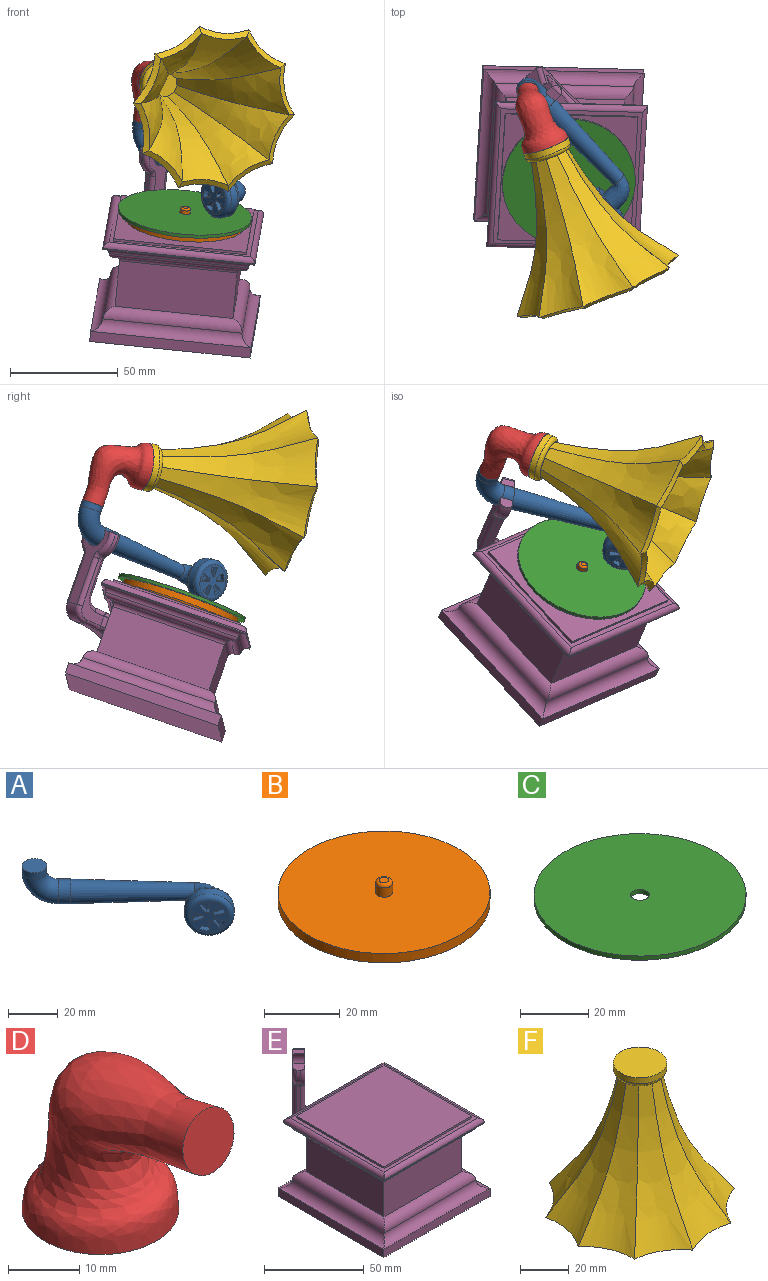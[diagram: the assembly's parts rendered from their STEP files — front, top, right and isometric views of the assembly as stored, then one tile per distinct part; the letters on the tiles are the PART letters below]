
ASSEMBLY  parts=6 mates=4
PART A: 36 faces, bbox 59.3x74.5x23.5 mm
  f0: plane 16x11.31mm, normal (-0.71,-0.71,0), area 140.5mm2, adj f9,f11,f12,f13,f14,f16,f17,f18
  f1: plane 10x10mm, normal (0,0,1), area 78.5mm2, adj f2
  f2: cylinder r=5mm len=10mm, axis (0,0,-1), area 89.1mm2, adj f1,f3
  f3: torus R=9.8mm, axis (-0.71,-0.71,0), area 483.5mm2, adj f2,f4
  f4: cylinder r=5mm len=10.53mm, axis (0.71,-0.71,0), area 153.6mm2, adj f3,f5
  f5: cone r=5mm half-angle=1.7deg, axis (-0.71,0.71,0), area 1335.8mm2, adj f4,f10
  f6: plane 16x11.31mm, normal (0.71,0.71,0), area 122.5mm2, adj f8,f10
  f7: cylinder r=10mm len=20mm, axis (0.71,0.71,0), area 251.3mm2, adj f8,f9
  f8: torus R=8mm, axis (0.71,0.71,0), area 183mm2, adj f6,f7
  f9: torus R=8mm, axis (0.71,0.71,0), area 183mm2, adj f0,f7
  f10: bspline ~17.32x14.96mm, area 372.1mm2, adj f5,f6
  f11: plane 3.64x3.57mm, normal (0.57,-0.57,0.59), area 10.8mm2, adj f0,f12,f14,f15
  f12: cylinder r=2.3mm len=2.55mm, axis (-0.71,-0.71,0), area 3.1mm2, adj f0,f11,f13,f15
  f13: plane 4.5x1.7mm, normal (-0.71,0.71,0), area 10.8mm2, adj f0,f12,f14,f15
  f14: cylinder r=6.8mm len=4.42mm, axis (-0.71,-0.71,0), area 9.9mm2, adj f0,f11,f13,f15
  f15: plane 4.89x2.72mm, normal (-0.71,-0.71,0), area 12.1mm2, adj f11,f12,f13,f14
  f16: plane 4.5x1.7mm, normal (-0.71,0.71,0), area 10.8mm2, adj f0,f17,f19,f20
  f17: cylinder r=2.3mm len=2.55mm, axis (-0.71,-0.71,0), area 3.1mm2, adj f0,f16,f18,f20
  f18: plane 3.64x3.57mm, normal (0.57,-0.57,-0.59), area 10.8mm2, adj f0,f17,f19,f20
  f19: cylinder r=6.8mm len=4.42mm, axis (-0.71,-0.71,0), area 9.9mm2, adj f0,f16,f18,f20
  f20: plane 4.89x2.72mm, normal (-0.71,-0.71,0), area 12.1mm2, adj f16,f17,f18,f19
  f21: plane 4.72x4.72mm, normal (-0.22,0.22,0.95), area 10.8mm2, adj f0,f22,f24,f25
  f22: cylinder r=2.3mm len=1.76mm, axis (-0.71,-0.71,0), area 3.1mm2, adj f0,f21,f23,f25
  f23: plane 4.72x4.72mm, normal (-0.22,0.22,-0.95), area 10.8mm2, adj f0,f22,f24,f25
  f24: cylinder r=6.8mm len=4.04mm, axis (-0.71,-0.71,0), area 9.9mm2, adj f0,f21,f23,f25
  f25: plane 4.04x3.24mm, normal (-0.71,-0.71,0), area 12.1mm2, adj f21,f22,f23,f24
  f26: plane 4.72x4.72mm, normal (-0.22,0.22,-0.95), area 10.8mm2, adj f0,f27,f29,f30
  f27: cylinder r=2.3mm len=2.22mm, axis (-0.71,-0.71,0), area 3.1mm2, adj f0,f26,f28,f30
  f28: plane 3.64x3.57mm, normal (0.57,-0.57,0.59), area 10.8mm2, adj f0,f27,f29,f30
  f29: cylinder r=6.8mm len=3.38mm, axis (-0.71,-0.71,0), area 9.9mm2, adj f0,f26,f28,f30
  f30: plane 4.66x3.55mm, normal (-0.71,-0.71,0), area 12.1mm2, adj f26,f27,f28,f29
  f31: plane 3.64x3.57mm, normal (0.57,-0.57,-0.59), area 10.8mm2, adj f0,f32,f34,f35
  f32: cylinder r=2.3mm len=2.22mm, axis (-0.71,-0.71,0), area 3.1mm2, adj f0,f31,f33,f35
  f33: plane 4.72x4.72mm, normal (-0.22,0.22,0.95), area 10.8mm2, adj f0,f32,f34,f35
  f34: cylinder r=6.8mm len=3.38mm, axis (-0.71,-0.71,0), area 9.9mm2, adj f0,f31,f33,f35
  f35: plane 4.66x3.55mm, normal (-0.71,-0.71,0), area 12.1mm2, adj f31,f32,f33,f34
PART B: 8 faces, bbox 56x56x8.2 mm
  f0: cylinder r=6mm len=12mm, axis (0,0,-1), area 45.2mm2, adj f1,f4
  f1: plane 12x12mm, normal (0,0,-1), area 113.1mm2, adj f0
  f2: cylinder r=28mm len=56mm, axis (0,0,-1), area 527.8mm2, adj f3,f4
  f3: plane 56x56mm, normal (0,0,1), area 2447.1mm2, adj f2,f5
  f4: plane 56x56mm, normal (0,0,-1), area 2349.9mm2, adj f0,f2
  f5: cylinder r=2.25mm len=4.5mm, axis (0,0,-1), area 42.4mm2, adj f3,f7
  f6: plane 2.5x2.5mm, normal (0,0,1), area 4.9mm2, adj f7
  f7: torus R=1.25mm, axis (0,0,1), area 18.6mm2, adj f5,f6
PART C: 4 faces, bbox 62x62x1.5 mm
  f0: cylinder r=2.75mm len=5.5mm, axis (0,0,-1), area 25.9mm2, adj f2,f3
  f1: cylinder r=31mm len=62mm, axis (0,0,-1), area 292.2mm2, adj f2,f3
  f2: plane 62x62mm, normal (0,0,1), area 2995.3mm2, adj f0,f1
  f3: plane 62x62mm, normal (0,0,-1), area 2995.3mm2, adj f0,f1
PART D: 3 faces, bbox 22x33.3x27.3 mm
  f0: plane 22x22mm, normal (0,0,-1), area 380.1mm2, adj f2
  f1: plane 10.01x9.86mm, normal (0,-0.98,0.17), area 78.5mm2, adj f2
  f2: bspline ~33.29x27.34mm, area 1810.4mm2, adj f0,f1
PART E: 88 faces, bbox 75.4x91.3x71.6 mm
  f0: plane 66x66mm, normal (0,0,1), area 512mm2, adj f35,f36,f37,f38,f39,f40,f41,f42
  f1: plane 75x5mm, normal (-1,0,0), area 375mm2, adj f2,f4,f5,f6
  f2: plane 75x5mm, normal (0,-1,0), area 375mm2, adj f1,f3,f5,f8
  f3: plane 75x5mm, normal (1,0,0), area 375mm2, adj f2,f4,f5,f9
  f4: plane 75x5mm, normal (0,1,0), area 375mm2, adj f1,f3,f5,f7
  f5: plane 75x75mm, normal (0,0,-1), area 5625mm2, adj f1,f2,f3,f4
  f6: cylinder r=5mm len=75mm, axis (0,-1,0), area 539mm2, adj f1,f7,f8,f14
  f7: cylinder r=5mm len=75mm, axis (-1,0,0), area 539mm2, adj f4,f6,f9,f15
  f8: cylinder r=5mm len=75mm, axis (1,0,0), area 539mm2, adj f2,f6,f9,f16
  f9: cylinder r=5mm len=75mm, axis (0,1,0), area 539mm2, adj f3,f7,f8,f17
  f10: plane 55x22.5mm, normal (1,0,0), area 1237.5mm2, adj f11,f13,f17,f21
  f11: plane 55x22.5mm, normal (0,1,0), area 970.8mm2, adj f10,f12,f15,f18,f68,f70,f71,f72
  f12: plane 55x22.5mm, normal (-1,0,0), area 1237.5mm2, adj f11,f13,f14,f19
  f13: plane 55x22.5mm, normal (0,-1,0), area 1237.5mm2, adj f10,f12,f16,f22
  f14: cylinder r=5mm len=65mm, axis (0,1,0), area 482mm2, adj f6,f12,f15,f16
  f15: cylinder r=5mm len=65mm, axis (1,0,0), area 482mm2, adj f7,f11,f14,f17
  f16: cylinder r=5mm len=65mm, axis (-1,0,0), area 482mm2, adj f8,f13,f14,f17
  f17: cylinder r=5mm len=65mm, axis (0,-1,0), area 482mm2, adj f9,f10,f15,f16
  f18: cylinder r=2.5mm len=60mm, axis (1,0,0), area 223.1mm2, adj f11,f19,f20,f21
  f19: cylinder r=2.5mm len=60mm, axis (0,1,0), area 223.1mm2, adj f12,f18,f22,f23
  f20: cylinder r=2.5mm len=64.98mm, axis (-1,0,0), area 233.3mm2, adj f18,f23,f24,f31
  f21: cylinder r=2.5mm len=60mm, axis (0,-1,0), area 223.1mm2, adj f10,f18,f22,f24
  f22: cylinder r=2.5mm len=60mm, axis (-1,0,0), area 223.1mm2, adj f13,f19,f21,f25
  f23: cylinder r=2.5mm len=64.98mm, axis (0,-1,0), area 233.3mm2, adj f19,f20,f25,f32
  f24: cylinder r=2.5mm len=64.98mm, axis (0,1,0), area 233.3mm2, adj f20,f21,f25,f33
  f25: cylinder r=2.5mm len=64.98mm, axis (1,0,0), area 233.3mm2, adj f22,f23,f24,f34
  f26: plane 71x0.5mm, normal (1,0,0), area 35.5mm2, adj f27,f29,f30,f35
  f27: plane 71x0.5mm, normal (0,1,0), area 35.5mm2, adj f26,f28,f30,f37
  f28: plane 71x0.5mm, normal (-1,0,0), area 35.5mm2, adj f27,f29,f30,f38
  f29: plane 71x0.5mm, normal (0,-1,0), area 35.5mm2, adj f26,f28,f30,f36
  f30: plane 71x71mm, normal (0,0,-1), area 6.5mm2, adj f26,f27,f28,f29,f31,f32,f33,f34
  f31: cylinder r=3mm len=70.95mm, axis (-1,0,0), area 298.6mm2, adj f20,f30,f32,f33
  f32: cylinder r=3mm len=70.95mm, axis (0,-1,0), area 298.6mm2, adj f23,f30,f31,f34
  f33: cylinder r=3mm len=70.95mm, axis (0,1,0), area 298.6mm2, adj f24,f30,f31,f34
  f34: cylinder r=3mm len=70.95mm, axis (1,0,0), area 298.6mm2, adj f25,f30,f32,f33
  f35: cylinder r=2.5mm len=71mm, axis (0,-1,0), area 271.7mm2, adj f0,f26,f36,f37
  f36: cylinder r=2.5mm len=71mm, axis (-1,0,0), area 271.7mm2, adj f0,f29,f35,f38
  f37: cylinder r=2.5mm len=71mm, axis (1,0,0), area 271.7mm2, adj f0,f27,f35,f38
  f38: cylinder r=2.5mm len=71mm, axis (0,1,0), area 271.7mm2, adj f0,f28,f36,f37
  f39: plane 62x1.2mm, normal (1,0,0), area 74.4mm2, adj f0,f40,f42,f43
  f40: plane 62x1.2mm, normal (0,1,0), area 74.4mm2, adj f0,f39,f41,f43
  f41: plane 62x1.2mm, normal (-1,0,0), area 74.4mm2, adj f0,f40,f42,f43
  f42: plane 62x1.2mm, normal (0,-1,0), area 74.4mm2, adj f0,f39,f41,f43
  f43: plane 62x62mm, normal (0,0,1), area 3844mm2, adj f39,f40,f41,f42
  f44: plane 15.31x11.06mm, normal (0,0,1), area 75.9mm2, adj f51,f69,f74,f79
  f45: cylinder r=59.47mm len=18.28mm, axis (-0.71,-0.71,0), area 101.3mm2, adj f48,f66,f71,f76
  f46: plane 31.84x20.25mm, normal (0.71,0.71,0), area 212.1mm2, adj f61,f62,f64,f65,f66,f67,f69,f70
  f47: plane 28.7x10.36mm, normal (-0.71,-0.71,0), area 123.1mm2, adj f75,f76,f78,f79,f80,f82,f84,f85
  f48: cylinder r=7.02mm len=9.45mm, axis (-0.71,-0.71,0), area 68.2mm2, adj f45,f49,f64,f78
  f49: plane 36.62x11.81mm, normal (-0.71,0.71,0), area 237.6mm2, adj f48,f52,f53,f54,f57,f59,f62,f80
  f50: plane 29.8x11.81mm, normal (0.71,-0.71,0), area 196.7mm2, adj f51,f52,f53,f54,f60,f63,f65,f84
  f51: cylinder r=5mm len=7.78mm, axis (-0.71,-0.71,0), area 47.1mm2, adj f44,f50,f67,f82
  f52: plane 7.62x7.62mm, normal (0,0,1), area 31.1mm2, adj f49,f50,f53,f56,f81,f87
  f53: cylinder r=5.35mm len=11.81mm, axis (-0.71,0.71,0), area 139.1mm2, adj f49,f50,f52,f54
  f54: plane 6.94x6.94mm, normal (0,0,1), area 23.1mm2, adj f49,f50,f53,f57,f58,f60
  f55: cylinder r=10.35mm len=9.77mm, axis (-0.71,0.71,0), area 22.5mm2, adj f57,f58,f60,f61
  f56: cylinder r=10.35mm len=11.53mm, axis (-0.71,0.71,0), area 26.1mm2, adj f52,f81,f85,f87
  f57: torus R=8.35mm, axis (0.71,-0.71,0), area 36.8mm2, adj f49,f54,f55,f58,f59
  f58: cylinder r=2mm len=5.57mm, axis (-0.71,0.71,0), area 11.4mm2, adj f54,f55,f57,f60
  f59: torus R=4mm, axis (0.71,-0.71,0), area 8.3mm2, adj f49,f57,f61,f62
  f60: torus R=8.35mm, axis (-0.71,0.71,0), area 36.8mm2, adj f50,f54,f55,f58,f63
  f61: cylinder r=2mm len=2.03mm, axis (-0.71,0.71,0), area 3.9mm2, adj f46,f55,f59,f63
  f62: cylinder r=2mm len=23.44mm, axis (0,0,-1), area 73.6mm2, adj f46,f49,f59,f64
  f63: torus R=4mm, axis (-0.71,0.71,0), area 8.3mm2, adj f50,f60,f61,f65
  f64: torus R=5.02mm, axis (0.71,0.71,0), area 32mm2, adj f46,f48,f62,f66
  f65: cylinder r=2mm len=16.63mm, axis (0,0,1), area 52.2mm2, adj f46,f50,f63,f67
  f66: torus R=61.47mm, axis (0.71,0.71,0), area 71mm2, adj f45,f46,f64,f68
  f67: torus R=7mm, axis (0.71,0.71,0), area 28.3mm2, adj f46,f51,f65,f69
  f68: bspline ~6.66x3.29mm, area 11.3mm2, adj f11,f66,f70,f71
  f69: cylinder r=2mm len=15.31mm, axis (-0.71,0.71,0), area 57.1mm2, adj f44,f46,f67,f72
  f70: cylinder r=2mm len=8.21mm, axis (0,0,1), area 12.9mm2, adj f11,f46,f68,f72
  f71: bspline ~8.89x3.4mm, area 24.4mm2, adj f11,f45,f68,f73
  f72: bspline ~6.64x4.7mm, area 13.9mm2, adj f11,f69,f70,f74
  f73: bspline ~6.37x5.35mm, area 22.4mm2, adj f11,f71,f75,f76
  f74: cylinder r=2mm len=8.49mm, axis (-1,0,0), area 26.7mm2, adj f11,f44,f72,f77
  f75: cylinder r=2mm len=5.08mm, axis (0,0,-1), area 23.9mm2, adj f11,f47,f73,f77
  f76: torus R=61.47mm, axis (0.71,0.71,0), area 34.5mm2, adj f45,f47,f73,f78
  f77: bspline ~5.66x4mm, area 21.5mm2, adj f11,f74,f75,f79
  f78: torus R=5.02mm, axis (0.71,0.71,0), area 32mm2, adj f47,f48,f76,f80
  f79: cylinder r=2mm len=8.23mm, axis (0.71,-0.71,0), area 22.3mm2, adj f44,f47,f77,f82
  f80: cylinder r=2mm len=23.44mm, axis (0,0,1), area 73.6mm2, adj f47,f49,f78,f83
  f81: torus R=8.35mm, axis (0.71,-0.71,0), area 39.2mm2, adj f49,f52,f56,f83
  f82: torus R=7mm, axis (0.71,0.71,0), area 28.3mm2, adj f47,f51,f79,f84
  f83: torus R=4mm, axis (0.71,-0.71,0), area 8.3mm2, adj f49,f80,f81,f85
  f84: cylinder r=2mm len=16.63mm, axis (0,0,-1), area 52.2mm2, adj f47,f50,f82,f86
  f85: cylinder r=2mm len=2.03mm, axis (-0.71,0.71,0), area 3.9mm2, adj f47,f56,f83,f86
  f86: torus R=4mm, axis (-0.71,0.71,0), area 8.3mm2, adj f50,f84,f85,f87
  f87: torus R=8.35mm, axis (-0.71,0.71,0), area 39.2mm2, adj f50,f52,f56,f86
PART F: 44 faces, bbox 89.9x89.8x78.5 mm
  f0: plane 4.7x2.76mm, normal (0,0,-1), area 1.4mm2, adj f15,f43
  f1: plane 4.97x2.24mm, normal (0,0,-1), area 1.4mm2, adj f14,f43
  f2: plane 5.3x1.24mm, normal (0,0,-1), area 1.4mm2, adj f13,f43
  f3: plane 4.06x3.64mm, normal (0,0,-1), area 1.4mm2, adj f12,f43
  f4: plane 5.4x0.8mm, normal (0,0,-1), area 1.4mm2, adj f11,f43
  f5: plane 4.7x2.76mm, normal (0,0,-1), area 1.4mm2, adj f10,f43
  f6: plane 4.97x2.24mm, normal (0,0,-1), area 1.4mm2, adj f9,f43
  f7: plane 5.3x1.24mm, normal (0,0,-1), area 1.4mm2, adj f17,f43
  f8: plane 4.06x3.64mm, normal (0,0,-1), area 1.4mm2, adj f18,f43
  f9: offset ~76x44.42mm, area 951.2mm2, adj f6,f10,f17,f37,f43
  f10: offset ~76x44.87mm, area 951.2mm2, adj f5,f9,f11,f38,f43
  f11: offset ~76x42.72mm, area 951.2mm2, adj f4,f10,f12,f29,f43
  f12: offset ~76x44.44mm, area 951.2mm2, adj f3,f11,f13,f30,f43
  f13: offset ~76x42.39mm, area 951.2mm2, adj f2,f12,f14,f31,f43
  f14: offset ~76x44.42mm, area 951.2mm2, adj f1,f13,f15,f32,f43
  f15: offset ~76x44.87mm, area 951.2mm2, adj f0,f14,f16,f33,f43
  f16: offset ~76x42.72mm, area 951.2mm2, adj f15,f18,f34,f41,f43
  f17: offset ~76x42.39mm, area 951.2mm2, adj f7,f9,f18,f36,f43
  f18: offset ~76x44.44mm, area 951.2mm2, adj f8,f16,f17,f35,f43
  f19: bspline ~70x32.87mm, area 827.5mm2, adj f20,f27,f37,f39
  f20: bspline ~70x32.65mm, area 827.5mm2, adj f19,f21,f38,f39
  f21: bspline ~70x31.34mm, area 827.5mm2, adj f20,f22,f29,f39
  f22: bspline ~67.5x30.92mm, area 827.5mm2, adj f21,f23,f30,f39
  f23: bspline ~67.5x31.78mm, area 827.5mm2, adj f22,f24,f31,f39
  f24: bspline ~70x32.87mm, area 827.5mm2, adj f23,f25,f32,f39
  f25: bspline ~70x32.65mm, area 827.5mm2, adj f24,f26,f33,f39
  f26: bspline ~70x31.34mm, area 827.5mm2, adj f25,f28,f34,f39
  f27: bspline ~67.5x31.78mm, area 827.5mm2, adj f19,f28,f36,f39
  f28: bspline ~67.5x30.92mm, area 827.5mm2, adj f26,f27,f35,f39
  f29: bspline ~24.73x6.52mm, area 73.3mm2, adj f11,f21,f30,f38
  f30: bspline ~19.82x18.19mm, area 73.3mm2, adj f12,f22,f29,f31
  f31: bspline ~24.3x8.33mm, area 73.3mm2, adj f13,f23,f30,f32
  f32: bspline ~23.06x12.44mm, area 73.3mm2, adj f14,f24,f31,f33
  f33: bspline ~22.16x14.63mm, area 73.3mm2, adj f15,f25,f32,f34
  f34: bspline ~24.73x6.52mm, area 73.3mm2, adj f16,f26,f33,f35
  f35: bspline ~19.82x18.19mm, area 73.3mm2, adj f18,f28,f34,f36
  f36: bspline ~24.3x8.33mm, area 73.3mm2, adj f17,f27,f35,f37
  f37: bspline ~23.06x12.44mm, area 73.3mm2, adj f9,f19,f36,f38
  f38: bspline ~22.16x14.63mm, area 73.3mm2, adj f10,f20,f29,f37
  f39: plane 11.58x11.38mm, normal (0,0,-1), area 99.4mm2, adj f19,f20,f21,f22,f23,f24,f25,f26
  f40: cylinder r=11mm len=22mm, axis (0,0,1), area 207.3mm2, adj f42,f43
  f41: plane 5.4x0.8mm, normal (0,0,-1), area 1.4mm2, adj f16,f43
  f42: plane 22x22mm, normal (0,0,1), area 380.1mm2, adj f40
  f43: torus R=9mm, axis (0,0,1), area 202.7mm2, adj f0,f1,f2,f3,f4,f5,f6,f7
PLACE A rot(axis=(0.95,0.28,-0.12),20.1deg) t=(-4.16,147.58,4.9)mm
PLACE B rot(axis=(0.95,0.28,-0.12),20.1deg) t=(-5.23,148.68,5.39)mm
PLACE C rot(axis=(0.95,0.28,-0.12),20.1deg) t=(-5.23,148.68,5.39)mm
PLACE D rot(axis=(0.12,-0.64,-0.76),165.9deg) t=(13.55,80.99,104.9)mm
PLACE E rot(axis=(0.95,0.28,-0.12),20.1deg) t=(-5.23,148.68,5.39)mm
PLACE F rot(axis=(0.12,-0.64,-0.76),165.9deg) t=(13.55,80.99,104.9)mm
MATE fastened D.f0 <-> F.f40  axis (0.34,-0.92,-0.17) through (-11.11,148.03,117.3)mm
MATE revolute C.f0 <-> B.f0  axis (-0.09,0.33,-0.94) through (-0.48,131.12,55.59)mm
MATE revolute A.f2 <-> D.f1  axis (0.09,-0.33,0.94) through (-19.38,172.42,100.02)mm
MATE revolute B.f0 <-> E.f43  axis (-0.09,0.33,-0.94) through (-0.85,132.5,51.64)mm
